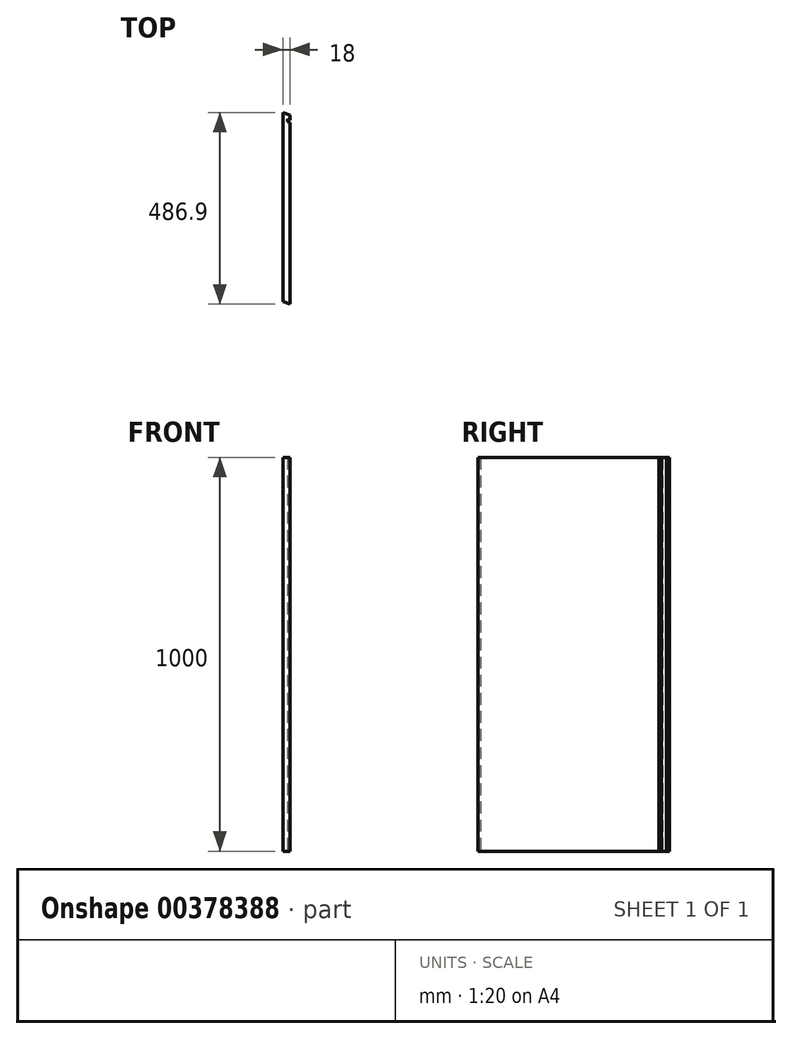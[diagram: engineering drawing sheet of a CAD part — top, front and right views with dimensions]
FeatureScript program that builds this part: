
annotation { "Feature Type Name" : "Feature", "Feature Type Description" : "" }
export const myFeature = defineFeature(function(context is Context, id is Id, definition is map)
    precondition{}
    {
        {
            var Q0;
            Q0=qCreatedBy(makeId("Top.planeOp"),FACE);
            var sketch = newSketch(context, id + "F0", { "sketchPlane" : qUnion([Q0])});
            skLineSegment(sketch, "E0.left", {"start": v(-9, 243.45) * mm, "end": v(-9, -236.55) * mm});
            skPoint(sketch, "E0.middle", {"position": v(0, 0) * mm});
            skLineSegment(sketch, "E1", {"start": v(-9, 243.45) * mm, "end": v(9, 236.55) * mm});
            skLineSegment(sketch, "E2", {"start": v(9, -243.45) * mm, "end": v(-9, -236.55) * mm});
            skLineSegment(sketch, "E3", {"start": v(9, 236.55) * mm, "end": v(9, 223.7) * mm});
            skLineSegment(sketch, "E4", {"start": v(9, 223.7) * mm, "end": v(3, 226) * mm});
            skLineSegment(sketch, "E5", {"start": v(3, 226) * mm, "end": v(3, 219.57) * mm});
            skLineSegment(sketch, "E6", {"start": v(3, 219.57) * mm, "end": v(9, 217.26) * mm});
            skLineSegment(sketch, "E7.trimOffspring", {"start": v(9, 217.26) * mm, "end": v(9, -243.45) * mm});
            skSolve(sketch);
        }
        {
            var Q0;
            Q0=qSketchRegion(id+"F0",true);
            extrude(context, id + "F1", {"entities" : qUnion([Q0]), "depth" : 1000 * mm});
        }
    });
